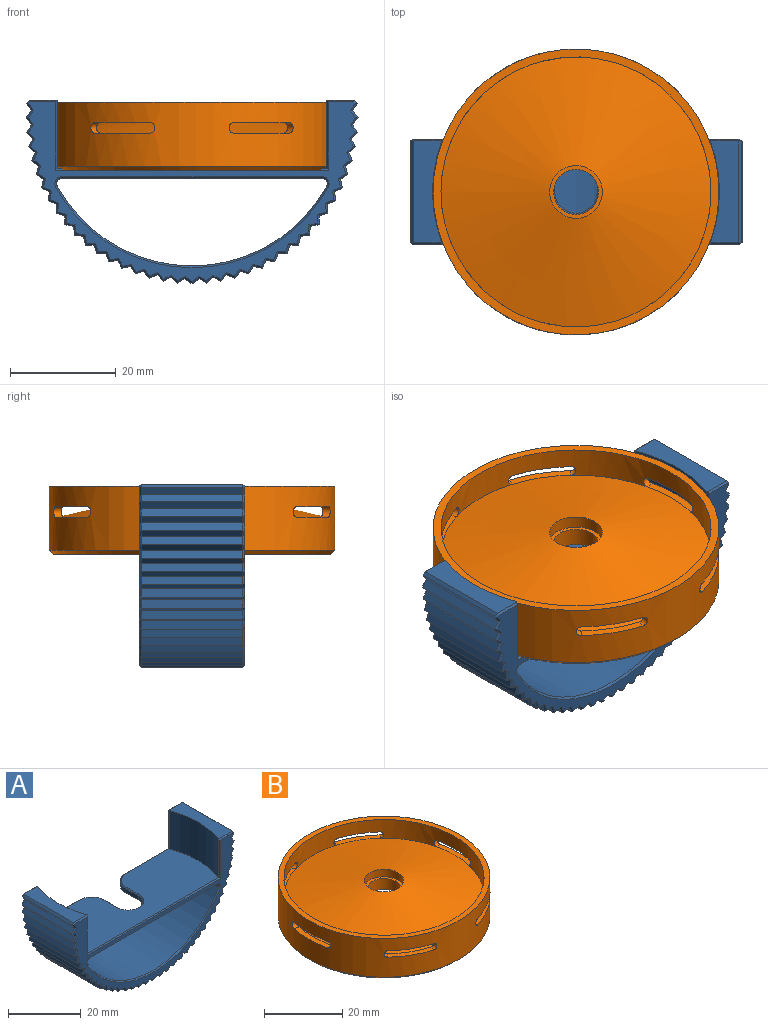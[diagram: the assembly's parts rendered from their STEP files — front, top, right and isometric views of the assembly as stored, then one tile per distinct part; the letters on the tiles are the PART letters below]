
ASSEMBLY  parts=2 mates=1
PART A: 280 faces, bbox 62.9x20x34.8 mm
  f0: plane 49.32x19.32mm, normal (0,0,-1), area 830mm2, adj f87,f88,f97,f98,f99,f100,f101,f102
  f1: plane 62.07x34.05mm, normal (0,-1,0), area 320.9mm2, adj f193,f194,f195,f196,f197,f198,f199,f200
  f2: plane 62.07x34.05mm, normal (0,1,0), area 298.1mm2, adj f92,f93,f94,f95,f96,f97,f98,f104
  f3: plane 19.32x5.32mm, normal (0,0,1), area 80.6mm2, adj f6,f85,f183,f185,f270,f272
  f4: plane 19.32x5.32mm, normal (0,0,1), area 80.6mm2, adj f5,f8,f182,f184,f276,f278
  f5: cylinder r=27.2mm len=19.08mm, axis (0,0,1), area 251.5mm2, adj f4,f7,f184,f276
  f6: cylinder r=27.2mm len=19.08mm, axis (0,0,1), area 251.5mm2, adj f3,f7,f185,f272
  f7: plane 54.4x19.32mm, normal (0,0,1), area 905.8mm2, adj f5,f6,f184,f185,f186,f187,f188,f189
  f8: plane 19.32x0.61mm, normal (0.74,0,0.67), area 15.9mm2, adj f4,f9,f180,f279
  f9: plane 19.32x1.41mm, normal (0.84,0,-0.54), area 32.3mm2, adj f8,f10,f178,f277
  f10: plane 19.32x1.33mm, normal (0.79,0,0.61), area 32.3mm2, adj f9,f11,f176,f275
  f11: plane 19.32x1.33mm, normal (0.79,0,-0.61), area 32.3mm2, adj f10,f12,f174,f273
  f12: plane 19.32x1.41mm, normal (0.84,0,0.54), area 32.3mm2, adj f11,f13,f172,f271
  f13: plane 19.32x1.24mm, normal (0.74,0,-0.67), area 32.3mm2, adj f12,f14,f170,f269
  f14: plane 19.32x1.49mm, normal (0.89,0,0.46), area 32.3mm2, adj f13,f15,f168,f267
  f15: plane 19.32x1.23mm, normal (0.68,0,-0.74), area 32.3mm2, adj f14,f16,f166,f265
  f16: plane 19.32x1.55mm, normal (0.92,0,0.38), area 32.3mm2, adj f15,f17,f164,f263
  f17: plane 19.32x1.33mm, normal (0.61,0,-0.79), area 32.3mm2, adj f16,f18,f162,f261
  f18: plane 19.32x1.6mm, normal (0.95,0,0.3), area 32.3mm2, adj f17,f19,f160,f259
  f19: plane 19.32x1.41mm, normal (0.54,0,-0.84), area 32.3mm2, adj f18,f20,f158,f257
  f20: plane 19.32x1.64mm, normal (0.98,0,0.22), area 32.3mm2, adj f19,f21,f156,f255
  f21: plane 19.32x1.48mm, normal (0.46,0,-0.89), area 32.3mm2, adj f20,f22,f154,f253
  f22: plane 19.32x1.66mm, normal (0.99,0,0.13), area 32.3mm2, adj f21,f23,f152,f251
  f23: plane 19.32x1.55mm, normal (0.38,0,-0.92), area 32.3mm2, adj f22,f24,f150,f249
  f24: plane 19.32x1.67mm, normal (1,0,0.04), area 32.3mm2, adj f23,f25,f148,f247
  f25: plane 19.32x1.6mm, normal (0.3,0,-0.95), area 32.3mm2, adj f24,f26,f146,f245
  f26: plane 19.32x1.67mm, normal (1,0,-0.04), area 32.3mm2, adj f25,f27,f144,f243
  f27: plane 19.32x1.63mm, normal (0.22,0,-0.98), area 32.3mm2, adj f26,f28,f142,f241
  f28: plane 19.32x1.66mm, normal (0.99,0,-0.13), area 32.3mm2, adj f27,f29,f140,f239
  f29: plane 19.32x1.66mm, normal (0.13,0,-0.99), area 32.3mm2, adj f28,f30,f138,f237
  f30: plane 19.32x1.63mm, normal (0.98,0,-0.22), area 32.3mm2, adj f29,f31,f136,f235
  f31: plane 19.32x1.67mm, normal (0.04,0,-1), area 32.3mm2, adj f30,f32,f134,f233
  f32: plane 19.32x1.6mm, normal (0.95,0,-0.3), area 32.3mm2, adj f31,f33,f132,f231
  f33: plane 19.32x1.67mm, normal (-0.04,0,-1), area 32.3mm2, adj f32,f34,f130,f229
  f34: plane 19.32x1.55mm, normal (0.92,0,-0.38), area 32.3mm2, adj f33,f35,f128,f227
  f35: plane 19.32x1.66mm, normal (-0.13,0,-0.99), area 32.3mm2, adj f34,f36,f126,f225
  f36: plane 19.32x1.48mm, normal (0.89,0,-0.46), area 32.3mm2, adj f35,f37,f124,f223
  f37: plane 19.32x1.64mm, normal (-0.22,0,-0.98), area 32.3mm2, adj f36,f38,f122,f221
  f38: plane 19.32x1.41mm, normal (0.84,0,-0.54), area 32.3mm2, adj f37,f39,f120,f219
  f39: plane 19.32x1.6mm, normal (-0.3,0,-0.95), area 32.3mm2, adj f38,f40,f118,f217
  f40: plane 19.32x1.33mm, normal (0.79,0,-0.61), area 32.3mm2, adj f39,f41,f116,f215
  f41: plane 19.32x1.55mm, normal (-0.38,0,-0.92), area 32.3mm2, adj f40,f42,f114,f213
  f42: plane 19.32x1.23mm, normal (0.74,0,-0.68), area 32.3mm2, adj f41,f43,f112,f211
  f43: plane 19.32x1.49mm, normal (-0.46,0,-0.89), area 32.3mm2, adj f42,f44,f110,f209
  f44: plane 19.32x1.24mm, normal (0.67,0,-0.74), area 32.3mm2, adj f43,f45,f108,f207
  f45: plane 19.32x1.41mm, normal (-0.54,0,-0.84), area 32.3mm2, adj f44,f46,f106,f205
  f46: plane 19.32x1.33mm, normal (0.61,0,-0.79), area 32.3mm2, adj f45,f47,f104,f203
  f47: plane 19.32x1.33mm, normal (-0.61,0,-0.79), area 32.3mm2, adj f46,f48,f105,f201
  f48: plane 19.32x1.41mm, normal (0.54,0,-0.84), area 32.3mm2, adj f47,f49,f107,f199
  f49: plane 19.32x1.24mm, normal (-0.67,0,-0.74), area 32.3mm2, adj f48,f50,f109,f197
  f50: plane 19.32x1.49mm, normal (0.46,0,-0.89), area 32.3mm2, adj f49,f51,f111,f198
  f51: plane 19.32x1.23mm, normal (-0.74,0,-0.68), area 32.3mm2, adj f50,f52,f113,f200
  f52: plane 19.32x1.55mm, normal (0.38,0,-0.92), area 32.3mm2, adj f51,f53,f115,f202
  f53: plane 19.32x1.33mm, normal (-0.79,0,-0.61), area 32.3mm2, adj f52,f54,f117,f204
  f54: plane 19.32x1.6mm, normal (0.3,0,-0.95), area 32.3mm2, adj f53,f55,f119,f206
  f55: plane 19.32x1.41mm, normal (-0.84,0,-0.54), area 32.3mm2, adj f54,f56,f121,f208
  f56: plane 19.32x1.64mm, normal (0.22,0,-0.98), area 32.3mm2, adj f55,f57,f123,f210
  f57: plane 19.32x1.48mm, normal (-0.89,0,-0.46), area 32.3mm2, adj f56,f58,f125,f212
  f58: plane 19.32x1.66mm, normal (0.13,0,-0.99), area 32.3mm2, adj f57,f59,f127,f214
  f59: plane 19.32x1.55mm, normal (-0.92,0,-0.38), area 32.3mm2, adj f58,f60,f129,f216
  f60: plane 19.32x1.67mm, normal (0.04,0,-1), area 32.3mm2, adj f59,f61,f131,f218
  f61: plane 19.32x1.6mm, normal (-0.95,0,-0.3), area 32.3mm2, adj f60,f62,f133,f220
  f62: plane 19.32x1.67mm, normal (-0.04,0,-1), area 32.3mm2, adj f61,f63,f135,f222
  f63: plane 19.32x1.63mm, normal (-0.98,0,-0.22), area 32.3mm2, adj f62,f64,f137,f224
  f64: plane 19.32x1.66mm, normal (-0.13,0,-0.99), area 32.3mm2, adj f63,f65,f139,f226
  f65: plane 19.32x1.66mm, normal (-0.99,0,-0.13), area 32.3mm2, adj f64,f66,f141,f228
  f66: plane 19.32x1.63mm, normal (-0.22,0,-0.98), area 32.3mm2, adj f65,f67,f143,f230
  f67: plane 19.32x1.67mm, normal (-1,0,-0.04), area 32.3mm2, adj f66,f68,f145,f232
  f68: plane 19.32x1.6mm, normal (-0.3,0,-0.95), area 32.3mm2, adj f67,f69,f147,f234
  f69: plane 19.32x1.67mm, normal (-1,0,0.04), area 32.3mm2, adj f68,f70,f149,f236
  f70: plane 19.32x1.55mm, normal (-0.38,0,-0.92), area 32.3mm2, adj f69,f71,f151,f238
  f71: plane 19.32x1.66mm, normal (-0.99,0,0.13), area 32.3mm2, adj f70,f72,f153,f240
  f72: plane 19.32x1.48mm, normal (-0.46,0,-0.89), area 32.3mm2, adj f71,f73,f155,f242
  f73: plane 19.32x1.64mm, normal (-0.98,0,0.22), area 32.3mm2, adj f72,f74,f157,f244
  f74: plane 19.32x1.41mm, normal (-0.54,0,-0.84), area 32.3mm2, adj f73,f75,f159,f246
  f75: plane 19.32x1.6mm, normal (-0.95,0,0.3), area 32.3mm2, adj f74,f76,f161,f248
  f76: plane 19.32x1.33mm, normal (-0.61,0,-0.79), area 32.3mm2, adj f75,f77,f163,f250
  f77: plane 19.32x1.55mm, normal (-0.92,0,0.38), area 32.3mm2, adj f76,f78,f165,f252
  f78: plane 19.32x1.23mm, normal (-0.68,0,-0.74), area 32.3mm2, adj f77,f79,f167,f254
  f79: plane 19.32x1.49mm, normal (-0.89,0,0.46), area 32.3mm2, adj f78,f80,f169,f256
  f80: plane 19.32x1.24mm, normal (-0.74,0,-0.67), area 32.3mm2, adj f79,f81,f171,f258
  f81: plane 19.32x1.41mm, normal (-0.84,0,0.54), area 32.3mm2, adj f80,f82,f173,f260
  f82: plane 19.32x1.33mm, normal (-0.79,0,-0.61), area 32.3mm2, adj f81,f83,f175,f262
  f83: plane 19.32x1.33mm, normal (-0.79,0,0.61), area 32.3mm2, adj f82,f84,f177,f264
  f84: plane 19.32x1.41mm, normal (-0.84,0,-0.54), area 32.3mm2, adj f83,f85,f179,f266
  f85: plane 19.32x0.61mm, normal (-0.74,0,0.67), area 15.9mm2, adj f3,f84,f181,f268
  f86: cylinder r=29.16mm len=51.07mm, axis (0,-1,0), area 1201.8mm2, adj f87,f88,f94,f193
  f87: cylinder r=1mm len=19.32mm, axis (0,-1,0), area 40.1mm2, adj f0,f86,f96,f194
  f88: cylinder r=1mm len=19.32mm, axis (0,-1,0), area 40.1mm2, adj f0,f86,f95,f195
  f89: cylinder r=4mm len=8mm, axis (0,0,1), area 16mm2, adj f90,f91,f103,f192
  f90: plane 5x1.27mm, normal (1,0,0), area 6.4mm2, adj f89,f92,f102,f191
  f91: plane 5x1.27mm, normal (-1,0,0), area 6.4mm2, adj f89,f93,f101,f190
  f92: cylinder r=5mm len=5mm, axis (0,0,-1), area 10mm2, adj f2,f90,f100,f189
  f93: cylinder r=5mm len=5mm, axis (0,0,-1), area 10mm2, adj f2,f91,f99,f188
  f94: cone r=29.5mm half-angle=45deg, axis (0,1,0), area 30.1mm2, adj f2,f86,f95,f96
  f95: cone r=1.34mm half-angle=45deg, axis (0,1,0), area 1.2mm2, adj f2,f88,f94,f97
  f96: cone r=1.34mm half-angle=45deg, axis (0,1,0), area 1.2mm2, adj f2,f87,f94,f98
  f97: plane 15.66x0.34mm, normal (0,0.71,-0.71), area 7.5mm2, adj f0,f2,f95,f99
  f98: plane 15.66x0.34mm, normal (0,0.71,-0.71), area 7.5mm2, adj f0,f2,f96,f100
  f99: cone r=4.66mm half-angle=45deg, axis (0,0,1), area 3.6mm2, adj f0,f93,f97,f101
  f100: cone r=4.66mm half-angle=45deg, axis (0,0,1), area 3.6mm2, adj f0,f92,f98,f102
  f101: plane 5x0.34mm, normal (-0.71,0,-0.71), area 2.4mm2, adj f0,f91,f99,f103
  f102: plane 5x0.34mm, normal (0.71,0,-0.71), area 2.4mm2, adj f0,f90,f100,f103
  f103: cone r=4mm half-angle=45deg, axis (0,0,-1), area 6.3mm2, adj f0,f89,f101,f102
  f104: plane 1.43x1.33mm, normal (0.43,0.71,-0.56), area 0.8mm2, adj f2,f46,f105,f106
  f105: plane 1.43x1.33mm, normal (-0.43,0.71,-0.56), area 0.8mm2, adj f2,f47,f104,f107
  f106: plane 1.43x1.31mm, normal (-0.38,0.71,-0.6), area 0.8mm2, adj f2,f45,f104,f108
  f107: plane 1.43x1.31mm, normal (0.38,0.71,-0.6), area 0.8mm2, adj f2,f48,f105,f109
  f108: plane 1.54x1.27mm, normal (0.48,0.71,-0.52), area 0.8mm2, adj f2,f44,f106,f110
  f109: plane 1.54x1.27mm, normal (-0.48,0.71,-0.52), area 0.8mm2, adj f2,f49,f107,f111
  f110: plane 1.54x1.18mm, normal (-0.33,0.71,-0.63), area 0.8mm2, adj f2,f43,f108,f112
  f111: plane 1.54x1.18mm, normal (0.33,0.71,-0.63), area 0.8mm2, adj f2,f50,f109,f113
  f112: plane 1.64x1.21mm, normal (0.52,0.71,-0.48), area 0.8mm2, adj f2,f42,f110,f114
  f113: plane 1.64x1.21mm, normal (-0.52,0.71,-0.48), area 0.8mm2, adj f2,f51,f111,f115
  f114: plane 1.64x1.04mm, normal (-0.27,0.71,-0.65), area 0.8mm2, adj f2,f41,f112,f116
  f115: plane 1.64x1.04mm, normal (0.27,0.71,-0.65), area 0.8mm2, adj f2,f52,f113,f117
  f116: plane 1.72x1.13mm, normal (0.56,0.71,-0.43), area 0.8mm2, adj f2,f40,f114,f118
  f117: plane 1.72x1.13mm, normal (-0.56,0.71,-0.43), area 0.8mm2, adj f2,f53,f115,f119
  f118: plane 1.72x0.9mm, normal (-0.21,0.71,-0.67), area 0.8mm2, adj f2,f39,f116,f120
  f119: plane 1.72x0.9mm, normal (0.21,0.71,-0.67), area 0.8mm2, adj f2,f54,f117,f121
  f120: plane 1.79x1.05mm, normal (0.6,0.71,-0.38), area 0.8mm2, adj f2,f38,f118,f122
  f121: plane 1.79x1.05mm, normal (-0.6,0.71,-0.38), area 0.8mm2, adj f2,f55,f119,f123
  f122: plane 1.79x0.74mm, normal (-0.15,0.71,-0.69), area 0.8mm2, adj f2,f37,f120,f124
  f123: plane 1.79x0.74mm, normal (0.15,0.71,-0.69), area 0.8mm2, adj f2,f56,f121,f125
  f124: plane 1.85x0.96mm, normal (0.63,0.71,-0.33), area 0.8mm2, adj f2,f36,f122,f126
  f125: plane 1.85x0.96mm, normal (-0.63,0.71,-0.33), area 0.8mm2, adj f2,f57,f123,f127
  f126: plane 1.85x0.58mm, normal (-0.09,0.71,-0.7), area 0.8mm2, adj f2,f35,f124,f128
  f127: plane 1.85x0.58mm, normal (0.09,0.71,-0.7), area 0.8mm2, adj f2,f58,f125,f129
  f128: plane 1.9x0.86mm, normal (0.65,0.71,-0.27), area 0.8mm2, adj f2,f34,f126,f130
  f129: plane 1.9x0.86mm, normal (-0.65,0.71,-0.27), area 0.8mm2, adj f2,f59,f127,f131
  f130: plane 1.9x0.42mm, normal (-0.03,0.71,-0.71), area 0.8mm2, adj f2,f33,f128,f132
  f131: plane 1.9x0.42mm, normal (0.03,0.71,-0.71), area 0.8mm2, adj f2,f60,f129,f133
  f132: plane 1.93x0.75mm, normal (0.67,0.71,-0.21), area 0.8mm2, adj f2,f32,f130,f134
  f133: plane 1.93x0.75mm, normal (-0.67,0.71,-0.21), area 0.8mm2, adj f2,f61,f131,f135
  f134: plane 1.93x0.4mm, normal (0.03,0.71,-0.71), area 0.8mm2, adj f2,f31,f132,f136
  f135: plane 1.93x0.4mm, normal (-0.03,0.71,-0.71), area 0.8mm2, adj f2,f62,f133,f137
  f136: plane 1.94x0.64mm, normal (0.69,0.71,-0.15), area 0.8mm2, adj f2,f30,f134,f138
  f137: plane 1.94x0.64mm, normal (-0.69,0.71,-0.15), area 0.8mm2, adj f2,f63,f135,f139
  f138: plane 1.94x0.52mm, normal (0.09,0.71,-0.7), area 0.8mm2, adj f2,f29,f136,f140
  f139: plane 1.94x0.52mm, normal (-0.09,0.71,-0.7), area 0.8mm2, adj f2,f64,f137,f141
  f140: plane 1.94x0.52mm, normal (0.7,0.71,-0.09), area 0.8mm2, adj f2,f28,f138,f142
  f141: plane 1.94x0.52mm, normal (-0.7,0.71,-0.09), area 0.8mm2, adj f2,f65,f139,f143
  f142: plane 1.94x0.64mm, normal (0.15,0.71,-0.69), area 0.8mm2, adj f2,f27,f140,f144
  f143: plane 1.94x0.64mm, normal (-0.15,0.71,-0.69), area 0.8mm2, adj f2,f66,f141,f145
  f144: plane 1.93x0.4mm, normal (0.71,0.71,-0.03), area 0.8mm2, adj f2,f26,f142,f146
  f145: plane 1.93x0.4mm, normal (-0.71,0.71,-0.03), area 0.8mm2, adj f2,f67,f143,f147
  f146: plane 1.93x0.75mm, normal (0.21,0.71,-0.67), area 0.8mm2, adj f2,f25,f144,f148
  f147: plane 1.93x0.75mm, normal (-0.21,0.71,-0.67), area 0.8mm2, adj f2,f68,f145,f149
  f148: plane 1.9x0.42mm, normal (0.71,0.71,0.03), area 0.8mm2, adj f2,f24,f146,f150
  f149: plane 1.9x0.42mm, normal (-0.71,0.71,0.03), area 0.8mm2, adj f2,f69,f147,f151
  f150: plane 1.9x0.86mm, normal (0.27,0.71,-0.65), area 0.8mm2, adj f2,f23,f148,f152
  f151: plane 1.9x0.86mm, normal (-0.27,0.71,-0.65), area 0.8mm2, adj f2,f70,f149,f153
  f152: plane 1.85x0.58mm, normal (0.7,0.71,0.09), area 0.8mm2, adj f2,f22,f150,f154
  f153: plane 1.85x0.58mm, normal (-0.7,0.71,0.09), area 0.8mm2, adj f2,f71,f151,f155
  f154: plane 1.85x0.96mm, normal (0.33,0.71,-0.63), area 0.8mm2, adj f2,f21,f152,f156
  f155: plane 1.85x0.96mm, normal (-0.33,0.71,-0.63), area 0.8mm2, adj f2,f72,f153,f157
  f156: plane 1.79x0.74mm, normal (0.69,0.71,0.15), area 0.8mm2, adj f2,f20,f154,f158
  f157: plane 1.79x0.74mm, normal (-0.69,0.71,0.15), area 0.8mm2, adj f2,f73,f155,f159
  f158: plane 1.79x1.05mm, normal (0.38,0.71,-0.6), area 0.8mm2, adj f2,f19,f156,f160
  f159: plane 1.79x1.05mm, normal (-0.38,0.71,-0.6), area 0.8mm2, adj f2,f74,f157,f161
  f160: plane 1.72x0.9mm, normal (0.67,0.71,0.21), area 0.8mm2, adj f2,f18,f158,f162
  f161: plane 1.72x0.9mm, normal (-0.67,0.71,0.21), area 0.8mm2, adj f2,f75,f159,f163
  f162: plane 1.72x1.13mm, normal (0.43,0.71,-0.56), area 0.8mm2, adj f2,f17,f160,f164
  f163: plane 1.72x1.13mm, normal (-0.43,0.71,-0.56), area 0.8mm2, adj f2,f76,f161,f165
  f164: plane 1.64x1.04mm, normal (0.65,0.71,0.27), area 0.8mm2, adj f2,f16,f162,f166
  f165: plane 1.64x1.04mm, normal (-0.65,0.71,0.27), area 0.8mm2, adj f2,f77,f163,f167
  f166: plane 1.64x1.21mm, normal (0.48,0.71,-0.52), area 0.8mm2, adj f2,f15,f164,f168
  f167: plane 1.64x1.21mm, normal (-0.48,0.71,-0.52), area 0.8mm2, adj f2,f78,f165,f169
  f168: plane 1.54x1.18mm, normal (0.63,0.71,0.33), area 0.8mm2, adj f2,f14,f166,f170
  f169: plane 1.54x1.18mm, normal (-0.63,0.71,0.33), area 0.8mm2, adj f2,f79,f167,f171
  f170: plane 1.54x1.27mm, normal (0.52,0.71,-0.48), area 0.8mm2, adj f2,f13,f168,f172
  f171: plane 1.54x1.27mm, normal (-0.52,0.71,-0.48), area 0.8mm2, adj f2,f80,f169,f173
  f172: plane 1.43x1.31mm, normal (0.6,0.71,0.38), area 0.8mm2, adj f2,f12,f170,f174
  f173: plane 1.43x1.31mm, normal (-0.6,0.71,0.38), area 0.8mm2, adj f2,f81,f171,f175
  f174: plane 1.43x1.33mm, normal (0.56,0.71,-0.43), area 0.8mm2, adj f2,f11,f172,f176
  f175: plane 1.43x1.33mm, normal (-0.56,0.71,-0.43), area 0.8mm2, adj f2,f82,f173,f177
  f176: plane 1.43x1.33mm, normal (0.56,0.71,0.43), area 0.8mm2, adj f2,f10,f174,f178
  f177: plane 1.43x1.33mm, normal (-0.56,0.71,0.43), area 0.8mm2, adj f2,f83,f175,f179
  f178: plane 1.43x1.31mm, normal (0.6,0.71,-0.38), area 0.8mm2, adj f2,f9,f176,f180
  f179: plane 1.43x1.31mm, normal (-0.6,0.71,-0.38), area 0.8mm2, adj f2,f84,f177,f181
  f180: plane 0.71x0.65mm, normal (0.52,0.71,0.48), area 0.3mm2, adj f2,f8,f178,f182
  f181: plane 0.71x0.65mm, normal (-0.52,0.71,0.48), area 0.3mm2, adj f2,f85,f179,f183
  f182: plane 5.24x0.34mm, normal (0,0.71,0.71), area 2.4mm2, adj f2,f4,f180,f184
  f183: plane 5.24x0.34mm, normal (0,0.71,0.71), area 2.4mm2, adj f2,f3,f181,f185
  f184: plane 13.24x0.46mm, normal (-0.82,0.57,0), area 7.2mm2, adj f2,f4,f5,f7,f182,f186
  f185: plane 13.24x0.46mm, normal (0.82,0.57,0), area 7.2mm2, adj f2,f3,f6,f7,f183,f187
  f186: plane 16.79x0.34mm, normal (0,0.71,0.71), area 8mm2, adj f2,f7,f184,f188
  f187: plane 16.79x0.34mm, normal (0,0.71,0.71), area 8mm2, adj f2,f7,f185,f189
  f188: cone r=4.66mm half-angle=45deg, axis (0,0,-1), area 3.6mm2, adj f7,f93,f186,f190
  f189: cone r=4.66mm half-angle=45deg, axis (0,0,-1), area 3.6mm2, adj f7,f92,f187,f191
  f190: plane 5x0.34mm, normal (-0.71,0,0.71), area 2.4mm2, adj f7,f91,f188,f192
  f191: plane 5x0.34mm, normal (0.71,0,0.71), area 2.4mm2, adj f7,f90,f189,f192
  f192: cone r=4.34mm half-angle=45deg, axis (0,0,1), area 6.3mm2, adj f7,f89,f190,f191
  f193: cone r=29.5mm half-angle=45deg, axis (0,-1,0), area 30.1mm2, adj f1,f86,f194,f195
  f194: cone r=1.34mm half-angle=45deg, axis (0,-1,0), area 1.2mm2, adj f1,f87,f193,f196
  f195: cone r=1.34mm half-angle=45deg, axis (0,-1,0), area 1.2mm2, adj f1,f88,f193,f196
  f196: plane 49.32x0.34mm, normal (0,-0.71,-0.71), area 23.7mm2, adj f0,f1,f194,f195
  f197: plane 1.54x1.27mm, normal (-0.48,-0.71,-0.52), area 0.8mm2, adj f1,f49,f198,f199
  f198: plane 1.54x1.18mm, normal (0.33,-0.71,-0.63), area 0.8mm2, adj f1,f50,f197,f200
  f199: plane 1.43x1.31mm, normal (0.38,-0.71,-0.6), area 0.8mm2, adj f1,f48,f197,f201
  f200: plane 1.64x1.21mm, normal (-0.52,-0.71,-0.48), area 0.8mm2, adj f1,f51,f198,f202
  f201: plane 1.43x1.33mm, normal (-0.43,-0.71,-0.56), area 0.8mm2, adj f1,f47,f199,f203
  f202: plane 1.64x1.04mm, normal (0.27,-0.71,-0.65), area 0.8mm2, adj f1,f52,f200,f204
  f203: plane 1.43x1.33mm, normal (0.43,-0.71,-0.56), area 0.8mm2, adj f1,f46,f201,f205
  f204: plane 1.72x1.13mm, normal (-0.56,-0.71,-0.43), area 0.8mm2, adj f1,f53,f202,f206
  f205: plane 1.43x1.31mm, normal (-0.38,-0.71,-0.6), area 0.8mm2, adj f1,f45,f203,f207
  f206: plane 1.72x0.9mm, normal (0.21,-0.71,-0.67), area 0.8mm2, adj f1,f54,f204,f208
  f207: plane 1.54x1.27mm, normal (0.48,-0.71,-0.52), area 0.8mm2, adj f1,f44,f205,f209
  f208: plane 1.79x1.05mm, normal (-0.6,-0.71,-0.38), area 0.8mm2, adj f1,f55,f206,f210
  f209: plane 1.54x1.18mm, normal (-0.33,-0.71,-0.63), area 0.8mm2, adj f1,f43,f207,f211
  f210: plane 1.79x0.74mm, normal (0.15,-0.71,-0.69), area 0.8mm2, adj f1,f56,f208,f212
  f211: plane 1.64x1.21mm, normal (0.52,-0.71,-0.48), area 0.8mm2, adj f1,f42,f209,f213
  f212: plane 1.85x0.96mm, normal (-0.63,-0.71,-0.33), area 0.8mm2, adj f1,f57,f210,f214
  f213: plane 1.64x1.04mm, normal (-0.27,-0.71,-0.65), area 0.8mm2, adj f1,f41,f211,f215
  f214: plane 1.85x0.58mm, normal (0.09,-0.71,-0.7), area 0.8mm2, adj f1,f58,f212,f216
  f215: plane 1.72x1.13mm, normal (0.56,-0.71,-0.43), area 0.8mm2, adj f1,f40,f213,f217
  f216: plane 1.9x0.86mm, normal (-0.65,-0.71,-0.27), area 0.8mm2, adj f1,f59,f214,f218
  f217: plane 1.72x0.9mm, normal (-0.21,-0.71,-0.67), area 0.8mm2, adj f1,f39,f215,f219
  f218: plane 1.9x0.42mm, normal (0.03,-0.71,-0.71), area 0.8mm2, adj f1,f60,f216,f220
  f219: plane 1.79x1.05mm, normal (0.6,-0.71,-0.38), area 0.8mm2, adj f1,f38,f217,f221
  f220: plane 1.93x0.75mm, normal (-0.67,-0.71,-0.21), area 0.8mm2, adj f1,f61,f218,f222
  f221: plane 1.79x0.74mm, normal (-0.15,-0.71,-0.69), area 0.8mm2, adj f1,f37,f219,f223
  f222: plane 1.93x0.4mm, normal (-0.03,-0.71,-0.71), area 0.8mm2, adj f1,f62,f220,f224
  f223: plane 1.85x0.96mm, normal (0.63,-0.71,-0.33), area 0.8mm2, adj f1,f36,f221,f225
  f224: plane 1.94x0.64mm, normal (-0.69,-0.71,-0.15), area 0.8mm2, adj f1,f63,f222,f226
  f225: plane 1.85x0.58mm, normal (-0.09,-0.71,-0.7), area 0.8mm2, adj f1,f35,f223,f227
  f226: plane 1.94x0.52mm, normal (-0.09,-0.71,-0.7), area 0.8mm2, adj f1,f64,f224,f228
  f227: plane 1.9x0.86mm, normal (0.65,-0.71,-0.27), area 0.8mm2, adj f1,f34,f225,f229
  f228: plane 1.94x0.52mm, normal (-0.7,-0.71,-0.09), area 0.8mm2, adj f1,f65,f226,f230
  f229: plane 1.9x0.42mm, normal (-0.03,-0.71,-0.71), area 0.8mm2, adj f1,f33,f227,f231
  f230: plane 1.94x0.64mm, normal (-0.15,-0.71,-0.69), area 0.8mm2, adj f1,f66,f228,f232
  f231: plane 1.93x0.75mm, normal (0.67,-0.71,-0.21), area 0.8mm2, adj f1,f32,f229,f233
  f232: plane 1.93x0.4mm, normal (-0.71,-0.71,-0.03), area 0.8mm2, adj f1,f67,f230,f234
  f233: plane 1.93x0.4mm, normal (0.03,-0.71,-0.71), area 0.8mm2, adj f1,f31,f231,f235
  f234: plane 1.93x0.75mm, normal (-0.21,-0.71,-0.67), area 0.8mm2, adj f1,f68,f232,f236
  f235: plane 1.94x0.64mm, normal (0.69,-0.71,-0.15), area 0.8mm2, adj f1,f30,f233,f237
  f236: plane 1.9x0.42mm, normal (-0.71,-0.71,0.03), area 0.8mm2, adj f1,f69,f234,f238
  f237: plane 1.94x0.52mm, normal (0.09,-0.71,-0.7), area 0.8mm2, adj f1,f29,f235,f239
  f238: plane 1.9x0.86mm, normal (-0.27,-0.71,-0.65), area 0.8mm2, adj f1,f70,f236,f240
  f239: plane 1.94x0.52mm, normal (0.7,-0.71,-0.09), area 0.8mm2, adj f1,f28,f237,f241
  f240: plane 1.85x0.58mm, normal (-0.7,-0.71,0.09), area 0.8mm2, adj f1,f71,f238,f242
  f241: plane 1.94x0.64mm, normal (0.15,-0.71,-0.69), area 0.8mm2, adj f1,f27,f239,f243
  f242: plane 1.85x0.96mm, normal (-0.33,-0.71,-0.63), area 0.8mm2, adj f1,f72,f240,f244
  f243: plane 1.93x0.4mm, normal (0.71,-0.71,-0.03), area 0.8mm2, adj f1,f26,f241,f245
  f244: plane 1.79x0.74mm, normal (-0.69,-0.71,0.15), area 0.8mm2, adj f1,f73,f242,f246
  f245: plane 1.93x0.75mm, normal (0.21,-0.71,-0.67), area 0.8mm2, adj f1,f25,f243,f247
  f246: plane 1.79x1.05mm, normal (-0.38,-0.71,-0.6), area 0.8mm2, adj f1,f74,f244,f248
  f247: plane 1.9x0.42mm, normal (0.71,-0.71,0.03), area 0.8mm2, adj f1,f24,f245,f249
  f248: plane 1.72x0.9mm, normal (-0.67,-0.71,0.21), area 0.8mm2, adj f1,f75,f246,f250
  f249: plane 1.9x0.86mm, normal (0.27,-0.71,-0.65), area 0.8mm2, adj f1,f23,f247,f251
  f250: plane 1.72x1.13mm, normal (-0.43,-0.71,-0.56), area 0.8mm2, adj f1,f76,f248,f252
  f251: plane 1.85x0.58mm, normal (0.7,-0.71,0.09), area 0.8mm2, adj f1,f22,f249,f253
  f252: plane 1.64x1.04mm, normal (-0.65,-0.71,0.27), area 0.8mm2, adj f1,f77,f250,f254
  f253: plane 1.85x0.96mm, normal (0.33,-0.71,-0.63), area 0.8mm2, adj f1,f21,f251,f255
  f254: plane 1.64x1.21mm, normal (-0.48,-0.71,-0.52), area 0.8mm2, adj f1,f78,f252,f256
  f255: plane 1.79x0.74mm, normal (0.69,-0.71,0.15), area 0.8mm2, adj f1,f20,f253,f257
  f256: plane 1.54x1.18mm, normal (-0.63,-0.71,0.33), area 0.8mm2, adj f1,f79,f254,f258
  f257: plane 1.79x1.05mm, normal (0.38,-0.71,-0.6), area 0.8mm2, adj f1,f19,f255,f259
  f258: plane 1.54x1.27mm, normal (-0.52,-0.71,-0.48), area 0.8mm2, adj f1,f80,f256,f260
  f259: plane 1.72x0.9mm, normal (0.67,-0.71,0.21), area 0.8mm2, adj f1,f18,f257,f261
  f260: plane 1.43x1.31mm, normal (-0.6,-0.71,0.38), area 0.8mm2, adj f1,f81,f258,f262
  f261: plane 1.72x1.13mm, normal (0.43,-0.71,-0.56), area 0.8mm2, adj f1,f17,f259,f263
  f262: plane 1.43x1.33mm, normal (-0.56,-0.71,-0.43), area 0.8mm2, adj f1,f82,f260,f264
  f263: plane 1.64x1.04mm, normal (0.65,-0.71,0.27), area 0.8mm2, adj f1,f16,f261,f265
  f264: plane 1.43x1.33mm, normal (-0.56,-0.71,0.43), area 0.8mm2, adj f1,f83,f262,f266
  f265: plane 1.64x1.21mm, normal (0.48,-0.71,-0.52), area 0.8mm2, adj f1,f15,f263,f267
  f266: plane 1.43x1.31mm, normal (-0.6,-0.71,-0.38), area 0.8mm2, adj f1,f84,f264,f268
  f267: plane 1.54x1.18mm, normal (0.63,-0.71,0.33), area 0.8mm2, adj f1,f14,f265,f269
  f268: plane 0.71x0.65mm, normal (-0.52,-0.71,0.48), area 0.3mm2, adj f1,f85,f266,f270
  f269: plane 1.54x1.27mm, normal (0.52,-0.71,-0.48), area 0.8mm2, adj f1,f13,f267,f271
  f270: plane 5.24x0.34mm, normal (0,-0.71,0.71), area 2.4mm2, adj f1,f3,f268,f272
  f271: plane 1.43x1.31mm, normal (0.6,-0.71,0.38), area 0.8mm2, adj f1,f12,f269,f273
  f272: plane 13.24x0.46mm, normal (0.82,-0.57,0), area 7.2mm2, adj f1,f3,f6,f7,f270,f274
  f273: plane 1.43x1.33mm, normal (0.56,-0.71,-0.43), area 0.8mm2, adj f1,f11,f271,f275
  f274: plane 51.58x0.34mm, normal (0,-0.71,0.71), area 24.7mm2, adj f1,f7,f272,f276
  f275: plane 1.43x1.33mm, normal (0.56,-0.71,0.43), area 0.8mm2, adj f1,f10,f273,f277
  f276: plane 13.24x0.46mm, normal (-0.82,-0.57,0), area 7.2mm2, adj f1,f4,f5,f7,f274,f278
  f277: plane 1.43x1.31mm, normal (0.6,-0.71,-0.38), area 0.8mm2, adj f1,f9,f275,f279
  f278: plane 5.24x0.34mm, normal (0,-0.71,0.71), area 2.4mm2, adj f1,f4,f276,f279
  f279: plane 0.71x0.65mm, normal (0.52,-0.71,0.48), area 0.3mm2, adj f1,f8,f277,f278
PART B: 35 faces, bbox 54.2x54.2x12.9 mm
  f0: cylinder r=25.6mm len=51.2mm, axis (0,0,-1), area 785.3mm2, adj f1,f8,f12,f13,f14,f16,f17,f18
  f1: cone r=5mm half-angle=76.8deg, axis (0,0,-1), area 2034.5mm2, adj f0,f2,f11,f15,f19,f23,f27,f31
  f2: cylinder r=5mm len=10mm, axis (0,0,-1), area 73.8mm2, adj f1,f3
  f3: plane 10x10mm, normal (0,0,1), area 21.8mm2, adj f2,f4
  f4: cylinder r=4.25mm len=8.5mm, axis (0,0,-1), area 93.5mm2, adj f3,f5
  f5: plane 51.2x51.2mm, normal (0,0,-1), area 2002.1mm2, adj f4,f6
  f6: cylinder r=25.6mm len=51.2mm, axis (0,0,-1), area 844.5mm2, adj f5,f9
  f7: cylinder r=27.1mm len=54.2mm, axis (0,0,-1), area 1895.2mm2, adj f8,f10,f11,f12,f13,f14,f15,f16
  f8: plane 54.2x54.2mm, normal (0,0,1), area 248.3mm2, adj f0,f7
  f9: cone r=25.6mm half-angle=45deg, axis (0,0,-1), area 173.1mm2, adj f6,f10
  f10: cone r=26.35mm half-angle=45deg, axis (0,0,1), area 178.1mm2, adj f7,f9
  f11: plane 10.86x7.1mm, normal (0,0,1), area 17.7mm2, adj f1,f7,f13,f14
  f12: plane 10.86x7.1mm, normal (0,0,-1), area 17.7mm2, adj f0,f7,f13,f14
  f13: cylinder r=1mm len=2mm, axis (-0.71,-0.71,0), area 4.7mm2, adj f0,f7,f11,f12
  f14: cylinder r=1mm len=2mm, axis (-0.26,-0.97,0), area 4.7mm2, adj f0,f7,f11,f12
  f15: plane 10.86x7.1mm, normal (0,0,1), area 17.7mm2, adj f1,f7,f17,f18
  f16: plane 10.86x7.1mm, normal (0,0,-1), area 17.7mm2, adj f0,f7,f17,f18
  f17: cylinder r=1mm len=2mm, axis (0.26,-0.97,0), area 4.7mm2, adj f0,f7,f15,f16
  f18: cylinder r=1mm len=2mm, axis (0.71,-0.71,0), area 4.7mm2, adj f0,f7,f15,f16
  f19: plane 12.09x2.13mm, normal (0,0,1), area 17.7mm2, adj f1,f7,f21,f22
  f20: plane 12.09x2.13mm, normal (0,0,-1), area 17.7mm2, adj f0,f7,f21,f22
  f21: cylinder r=1mm len=2mm, axis (0.97,-0.26,0), area 4.7mm2, adj f0,f7,f19,f20
  f22: cylinder r=1mm len=2mm, axis (0.97,0.26,0), area 4.7mm2, adj f0,f7,f19,f20
  f23: plane 10.86x7.1mm, normal (0,0,1), area 17.7mm2, adj f1,f7,f25,f26
  f24: plane 10.86x7.1mm, normal (0,0,-1), area 17.7mm2, adj f0,f7,f25,f26
  f25: cylinder r=1mm len=2mm, axis (0.71,0.71,0), area 4.7mm2, adj f0,f7,f23,f24
  f26: cylinder r=1mm len=2mm, axis (0.26,0.97,0), area 4.7mm2, adj f0,f7,f23,f24
  f27: plane 10.86x7.1mm, normal (0,0,1), area 17.7mm2, adj f1,f7,f29,f30
  f28: plane 10.86x7.1mm, normal (0,0,-1), area 17.7mm2, adj f0,f7,f29,f30
  f29: cylinder r=1mm len=2mm, axis (-0.26,0.97,0), area 4.7mm2, adj f0,f7,f27,f28
  f30: cylinder r=1mm len=2mm, axis (-0.71,0.71,0), area 4.7mm2, adj f0,f7,f27,f28
  f31: plane 12.09x2.13mm, normal (0,0,1), area 17.7mm2, adj f1,f7,f33,f34
  f32: plane 12.09x2.13mm, normal (0,0,-1), area 17.7mm2, adj f0,f7,f33,f34
  f33: cylinder r=1mm len=2mm, axis (-0.97,0.26,0), area 4.7mm2, adj f0,f7,f31,f32
  f34: cylinder r=1mm len=2mm, axis (-0.97,-0.26,0), area 4.7mm2, adj f0,f7,f31,f32
PLACE A t=(-0.01,-3.66,18.47)mm
PLACE B t=(-0.01,-13.66,18.07)mm
MATE revolute B.f0 <-> A.f5  axis (0,0,-1) through (-0.01,-13.66,24.87)mm
